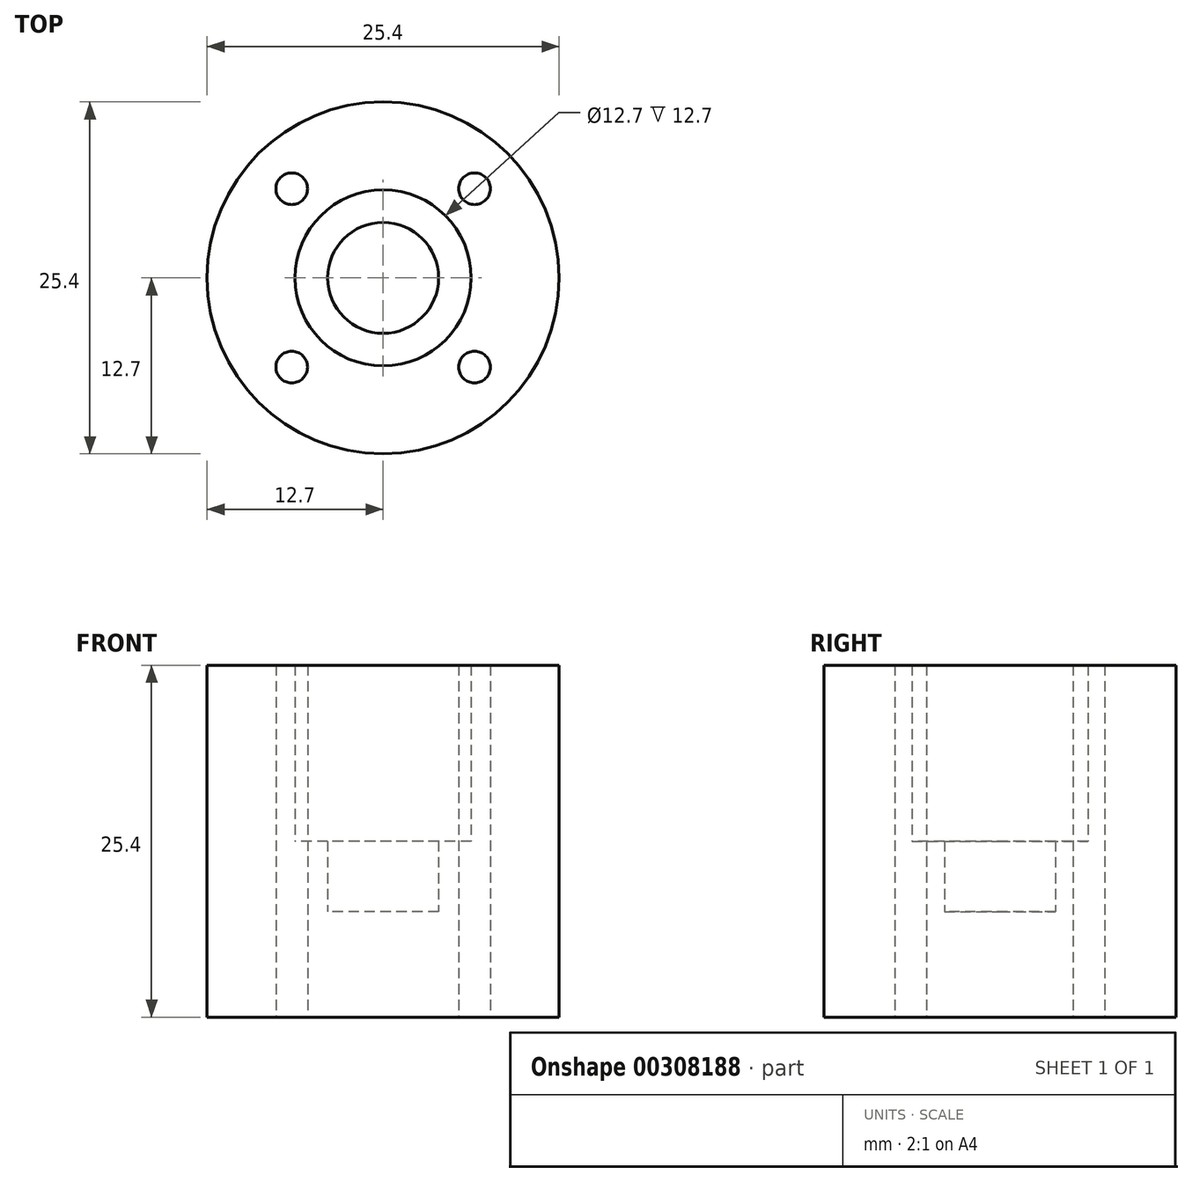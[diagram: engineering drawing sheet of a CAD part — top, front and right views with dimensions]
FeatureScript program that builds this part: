
annotation { "Feature Type Name" : "Feature", "Feature Type Description" : "" }
export const myFeature = defineFeature(function(context is Context, id is Id, definition is map)
    precondition{}
    {
        {
            var Q0;
            Q0=qCreatedBy(makeId("Top.planeOp"),FACE);
            var sketch = newSketch(context, id + "F0", { "sketchPlane" : qUnion([Q0])});
            skCircle(sketch, "E0", {"center": v(0, 0) * mm, "radius": 4 * mm});
            skCircle(sketch, "E1", {"center": v(0, 0) * mm, "radius": 12.7 * mm});
            skCircle(sketch, "E2", {"center": v(0, 0) * mm, "radius": 6.35 * mm});
            skCircle(sketch, "E3", {"center": v(-6.6, 6.44) * mm, "radius": 1.14 * mm});
            skCircle(sketch, "E4", {"center": v(6.6, 6.44) * mm, "radius": 1.14 * mm});
            skCircle(sketch, "E5", {"center": v(6.6, -6.44) * mm, "radius": 1.14 * mm});
            skCircle(sketch, "E6", {"center": v(-6.6, -6.44) * mm, "radius": 1.14 * mm});
            skSolve(sketch);
        }
        {
            var Q0;
            Q0 = qSketchRegion(id + "F0", true);
            extrude(context, id + "F1", {"entities" : qUnion([Q0]), "depth" : 25.4 * mm});
        }
        {
            var Q0;
            Q0=makeQuery(id+"F0.imprint","IMPRINT",FACE,{"disambiguationData":[TD([[makeQuery(id+"F0.imprint","IMPRINT",EDGE,{"derivedFrom":sQuery(id+"F0.wireOp",EDGE,"E0")}),-1.0]])]});
            extrude(context, id + "F2", {"entities" : qUnion([Q0]), "operationType" : NewBodyOperationType.ADD, "depth" : 12.7 * mm});
        }
        {
            var Q0;
            Q0=makeQuery(id+"F0.imprint","IMPRINT",FACE,{"disambiguationData":[TD([[makeQuery(id+"F0.imprint","IMPRINT",EDGE,{"derivedFrom":sQuery(id+"F0.wireOp",EDGE,"E0")}),1.0]])]});
            extrude(context, id + "F3", {"entities" : qUnion([Q0]), "operationType" : NewBodyOperationType.ADD, "depth" : 7.62 * mm});
        }
    });
